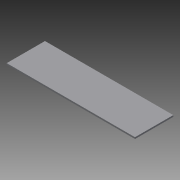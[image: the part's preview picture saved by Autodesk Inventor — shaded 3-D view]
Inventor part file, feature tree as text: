
AUTODESK INVENTOR PART (.ipt)
format: ipt  version: 2013 (Build 170138000, 138)  size: 64,512 bytes
history: native  units: mm
features: extrude x1, sketch x1
ambient origin geometry x8: Origin, YZ Plane, XZ Plane, XY Plane, X Axis, Y Axis, Z Axis, Center Point
bodies: Volumenkörper1 (feature_tree)
feature tree (2):
  extrude  "Extrusion1"  Depth=67.0mm
  sketch  "Skizze1"  dims[d0=20.0mm d2=67.0mm d3=0.8mm d4=0.0mm]
